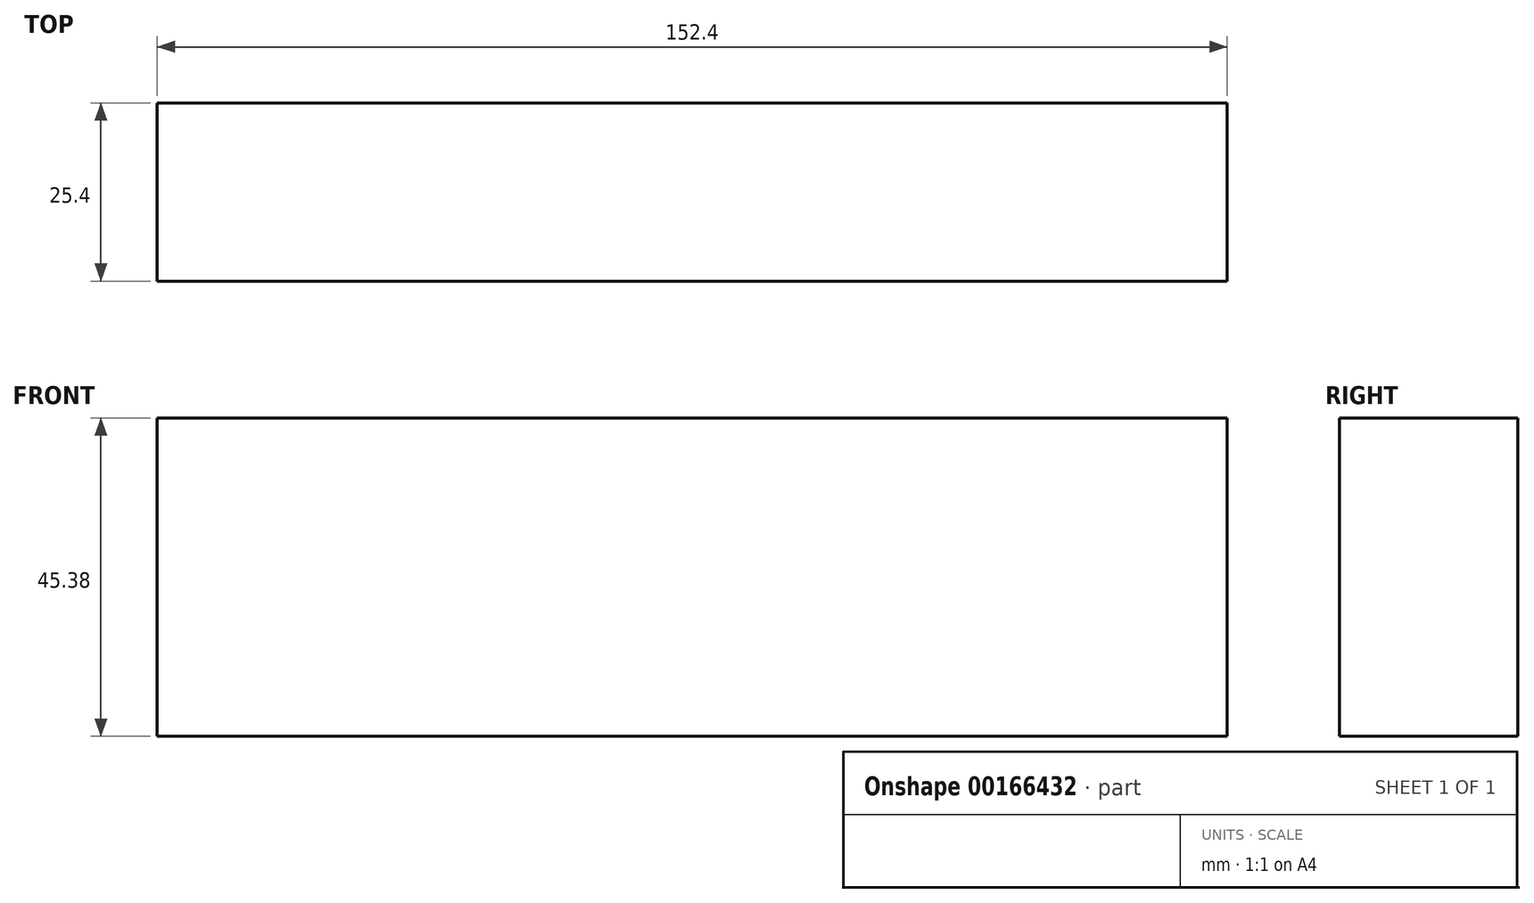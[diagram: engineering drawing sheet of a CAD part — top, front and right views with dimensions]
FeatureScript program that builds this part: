
annotation { "Feature Type Name" : "Feature", "Feature Type Description" : "" }
export const myFeature = defineFeature(function(context is Context, id is Id, definition is map)
    precondition{}
    {
        {
            var Q0;
            Q0=qCreatedBy(makeId("Front.planeOp"),FACE);
            var sketch = newSketch(context, id + "F0", { "sketchPlane" : qUnion([Q0])});
            skLineSegment(sketch, "E0.bottom", {"start": v(76.2, -22.7) * mm, "end": v(-76.2, -22.7) * mm});
            skLineSegment(sketch, "E0.top", {"start": v(76.2, 22.7) * mm, "end": v(-76.2, 22.7) * mm});
            skLineSegment(sketch, "E0.left", {"start": v(76.2, -22.7) * mm, "end": v(76.2, 22.7) * mm});
            skLineSegment(sketch, "E0.right", {"start": v(-76.2, -22.7) * mm, "end": v(-76.2, 22.7) * mm});
            skPoint(sketch, "E0.middle", {"position": v(0, 0) * mm});
            skSolve(sketch);
        }
        {
            var Q0;
            Q0 = qSketchRegion(id + "F0", true);
            extrude(context, id + "F1", {"entities" : qUnion([Q0]), "depth" : 25.4 * mm});
        }
    });
